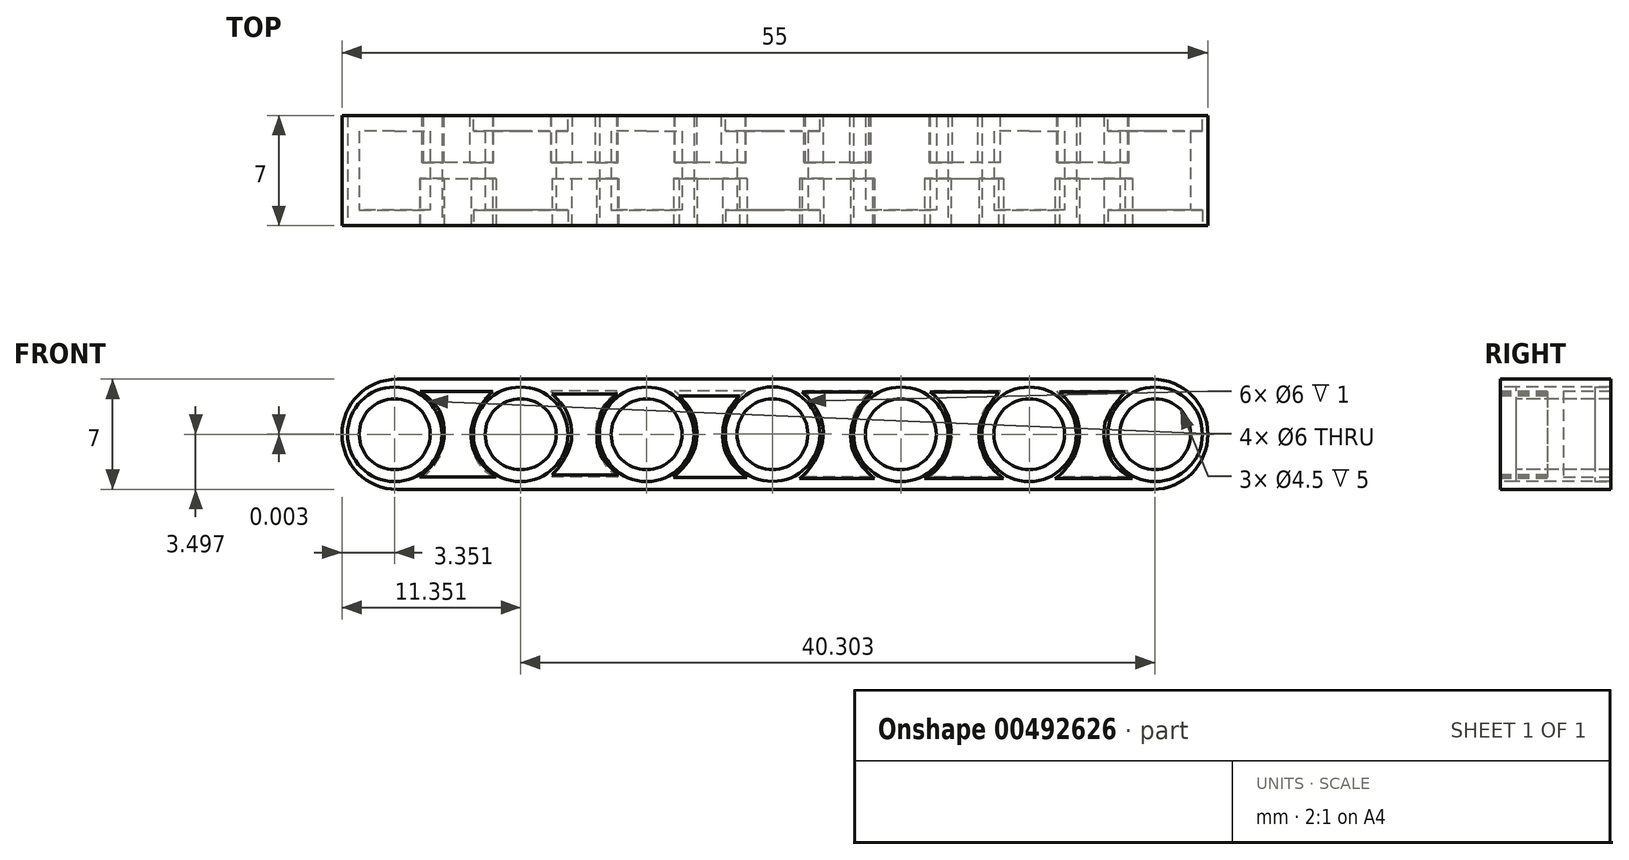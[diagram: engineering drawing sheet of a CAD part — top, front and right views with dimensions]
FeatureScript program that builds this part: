
annotation { "Feature Type Name" : "Feature", "Feature Type Description" : "" }
export const myFeature = defineFeature(function(context is Context, id is Id, definition is map)
    precondition{}
    {
        {
            var Q0;
            Q0=qCreatedBy(makeId("Front.planeOp"),FACE);
            var sketch = newSketch(context, id + "F0", { "sketchPlane" : qUnion([Q0])});
            skLineSegment(sketch, "E0", {"start": v(-51.8, 37) * mm, "end": v(3.2, 37) * mm});
            skLineSegment(sketch, "E1", {"start": v(3.2, 37) * mm, "end": v(3.2, 30) * mm});
            skLineSegment(sketch, "E2", {"start": v(3.2, 30) * mm, "end": v(-51.8, 30) * mm});
            skLineSegment(sketch, "E3", {"start": v(-51.8, 30) * mm, "end": v(-51.8, 37) * mm});
            skSolve(sketch);
        }
        {
            var Q0;
            Q0=makeQuery(id+"F0.imprint","IMPRINT",FACE,{"disambiguationData":[TD([[makeQuery(id+"F0.imprint","IMPRINT",EDGE,{"derivedFrom":sQuery(id+"F0.wireOp",EDGE,"E0")}),-1.0]])]});
            extrude(context, id + "F1", {"entities" : qUnion([Q0]), "depth" : 7 * mm});
        }
        {
            var Q0;
            Q0=makeQuery(id+"F1.opExtrude","CAP_FACE",FACE,{"disambiguationData":[OSD([sQuery(id+"F0.wireOp",EDGE,"E0"),sQuery(id+"F0.wireOp",EDGE,"E1"),sQuery(id+"F0.wireOp",EDGE,"E2"),sQuery(id+"F0.wireOp",EDGE,"E3")])],"isStart":false});
            var sketch = newSketch(context, id + "F2", { "sketchPlane" : qUnion([Q0])});
            skPoint(sketch, "E4.startSnap0", {"position": v(-51.8, 33.5) * mm});
            skCircle(sketch, "E5.MirrorC", {"center": v(-0.16, 33.5) * mm, "radius": 2.25 * mm});
            skCircle(sketch, "E6.MirrorC", {"center": v(-16.3, 33.5) * mm, "radius": 2.25 * mm});
            skCircle(sketch, "E7.MirrorC", {"center": v(-24.46, 33.5) * mm, "radius": 2.25 * mm});
            skCircle(sketch, "E8.MirrorC", {"center": v(-32.46, 33.5) * mm, "radius": 2.25 * mm});
            skCircle(sketch, "E9.MirrorC", {"center": v(-40.46, 33.5) * mm, "radius": 2.25 * mm});
            skCircle(sketch, "E10.MirrorC", {"center": v(-48.46, 33.5) * mm, "radius": 2.25 * mm});
            skCircle(sketch, "E11.MirrorC", {"center": v(-8.16, 33.5) * mm, "radius": 2.25 * mm});
            skCircle(sketch, "E12", {"center": v(-0.16, 33.5) * mm, "radius": 3 * mm});
            skCircle(sketch, "E13", {"center": v(-8.16, 33.5) * mm, "radius": 3 * mm});
            skCircle(sketch, "E14", {"center": v(-16.3, 33.5) * mm, "radius": 3 * mm});
            skCircle(sketch, "E15", {"center": v(-24.46, 33.5) * mm, "radius": 3 * mm});
            skCircle(sketch, "E16", {"center": v(-32.46, 33.5) * mm, "radius": 3 * mm});
            skCircle(sketch, "E17", {"center": v(-40.46, 33.5) * mm, "radius": 3 * mm});
            skCircle(sketch, "E18", {"center": v(-48.46, 33.5) * mm, "radius": 3 * mm});
            skSolve(sketch);
        }
        {
            var Q0;
            Q0=makeQuery(id+"F2.imprint","IMPRINT",FACE,{"disambiguationData":[TD([[makeQuery(id+"F2.imprint","IMPRINT",EDGE,{"derivedFrom":sQuery(id+"F2.wireOp",EDGE,"E10.MirrorC")}),-1.0]])]});
            var Q1;
            Q1=makeQuery(id+"F2.imprint","IMPRINT",FACE,{"disambiguationData":[TD([[makeQuery(id+"F2.imprint","IMPRINT",EDGE,{"derivedFrom":sQuery(id+"F2.wireOp",EDGE,"E9.MirrorC")}),1.0]])]});
            var Q2;
            Q2=makeQuery(id+"F2.imprint","IMPRINT",FACE,{"disambiguationData":[TD([[makeQuery(id+"F2.imprint","IMPRINT",EDGE,{"derivedFrom":sQuery(id+"F2.wireOp",EDGE,"E8.MirrorC")}),-1.0]])]});
            var Q3;
            Q3=makeQuery(id+"F2.imprint","IMPRINT",FACE,{"disambiguationData":[TD([[makeQuery(id+"F2.imprint","IMPRINT",EDGE,{"derivedFrom":sQuery(id+"F2.wireOp",EDGE,"E7.MirrorC")}),1.0]])]});
            var Q4;
            Q4=makeQuery(id+"F2.imprint","IMPRINT",FACE,{"disambiguationData":[TD([[makeQuery(id+"F2.imprint","IMPRINT",EDGE,{"derivedFrom":sQuery(id+"F2.wireOp",EDGE,"E6.MirrorC")}),-1.0]])]});
            var Q5;
            Q5=makeQuery(id+"F2.imprint","IMPRINT",FACE,{"disambiguationData":[TD([[makeQuery(id+"F2.imprint","IMPRINT",EDGE,{"derivedFrom":sQuery(id+"F2.wireOp",EDGE,"E11.MirrorC")}),-1.0]])]});
            var Q6;
            Q6=makeQuery(id+"F2.imprint","IMPRINT",FACE,{"disambiguationData":[TD([[makeQuery(id+"F2.imprint","IMPRINT",EDGE,{"derivedFrom":sQuery(id+"F2.wireOp",EDGE,"E5.MirrorC")}),1.0]])]});
            extrude(context, id + "F3", {"entities" : qUnion([Q0, Q1, Q2, Q3, Q4, Q5, Q6]), "operationType" : NewBodyOperationType.REMOVE, "oppositeDirection" : true, "depth" : 8 * mm});
        }
        {
            var Q0;
            Q0=makeQuery(id+"F1.opExtrude","CAP_FACE",FACE,{"disambiguationData":[OSD([sQuery(id+"F0.wireOp",EDGE,"E0"),sQuery(id+"F0.wireOp",EDGE,"E1"),sQuery(id+"F0.wireOp",EDGE,"E2"),sQuery(id+"F0.wireOp",EDGE,"E3")])],"isStart":false});
            var sketch = newSketch(context, id + "F4", { "sketchPlane" : qUnion([Q0])});
            skSolve(sketch);
        }
        {
            var Q0;
            Q0=makeQuery(id+"F1.opExtrude","SWEPT_EDGE",EDGE,{"disambiguationData":[OSD([sQuery(id+"F0.wireOp",EDGE,"E1"),sQuery(id+"F0.wireOp",EDGE,"E2")])]});
            var Q1;
            Q1=makeQuery(id+"F1.opExtrude","SWEPT_EDGE",EDGE,{"disambiguationData":[OSD([sQuery(id+"F0.wireOp",EDGE,"E0"),sQuery(id+"F0.wireOp",EDGE,"E1")])]});
            var Q2;
            Q2=makeQuery(id+"F1.opExtrude","SWEPT_EDGE",EDGE,{"disambiguationData":[OSD([sQuery(id+"F0.wireOp",EDGE,"E2"),sQuery(id+"F0.wireOp",EDGE,"E3")])]});
            var Q3;
            Q3=makeQuery(id+"F1.opExtrude","SWEPT_EDGE",EDGE,{"disambiguationData":[OSD([sQuery(id+"F0.wireOp",EDGE,"E0"),sQuery(id+"F0.wireOp",EDGE,"E3")])]});
            fillet(context, id + "F5", {"entities" : qUnion([Q0, Q1, Q2, Q3]), "radius" : 3.5 * mm, "tangentPropagation" : true, "allowEdgeOverflow" : false});
        }
        {
            var Q0;
            Q0=makeQuery(id+"F2.imprint","IMPRINT",FACE,{"disambiguationData":[TD([[makeQuery(id+"F2.imprint","IMPRINT",EDGE,{"derivedFrom":sQuery(id+"F2.wireOp",EDGE,"E10.MirrorC")}),1.0]])]});
            var Q1;
            Q1=makeQuery(id+"F2.imprint","IMPRINT",FACE,{"disambiguationData":[TD([[makeQuery(id+"F2.imprint","IMPRINT",EDGE,{"derivedFrom":sQuery(id+"F2.wireOp",EDGE,"E9.MirrorC")}),-1.0]])]});
            var Q2;
            Q2=makeQuery(id+"F2.imprint","IMPRINT",FACE,{"disambiguationData":[TD([[makeQuery(id+"F2.imprint","IMPRINT",EDGE,{"derivedFrom":sQuery(id+"F2.wireOp",EDGE,"E8.MirrorC")}),1.0]])]});
            var Q3;
            Q3=makeQuery(id+"F2.imprint","IMPRINT",FACE,{"disambiguationData":[TD([[makeQuery(id+"F2.imprint","IMPRINT",EDGE,{"derivedFrom":sQuery(id+"F2.wireOp",EDGE,"E7.MirrorC")}),-1.0]])]});
            var Q4;
            Q4=makeQuery(id+"F2.imprint","IMPRINT",FACE,{"disambiguationData":[TD([[makeQuery(id+"F2.imprint","IMPRINT",EDGE,{"derivedFrom":sQuery(id+"F2.wireOp",EDGE,"E6.MirrorC")}),1.0]])]});
            var Q5;
            Q5=makeQuery(id+"F2.imprint","IMPRINT",FACE,{"disambiguationData":[TD([[makeQuery(id+"F2.imprint","IMPRINT",EDGE,{"derivedFrom":sQuery(id+"F2.wireOp",EDGE,"E11.MirrorC")}),1.0]])]});
            var Q6;
            Q6=makeQuery(id+"F2.imprint","IMPRINT",FACE,{"disambiguationData":[TD([[makeQuery(id+"F2.imprint","IMPRINT",EDGE,{"derivedFrom":sQuery(id+"F2.wireOp",EDGE,"E5.MirrorC")}),-1.0]])]});
            extrude(context, id + "F6", {"entities" : qUnion([Q0, Q1, Q2, Q3, Q4, Q5, Q6]), "operationType" : NewBodyOperationType.REMOVE, "oppositeDirection" : true, "depth" : 1 * mm});
        }
        {
            var Q0;
            Q0=makeQuery(id+"F4.imprint","IMPRINT",FACE,{"disambiguationData":[TD([[makeQuery(id+"F4.imprint","IMPRINT",EDGE,{"derivedFrom":makeQuery(id+"F1.opExtrude","CAP_EDGE",EDGE,{"disambiguationData":[OSD([sQuery(id+"F0.wireOp",EDGE,"E0")])],"isStart":false})}),-1.0]])]});
            var sketch = newSketch(context, id + "F7", { "sketchPlane" : qUnion([Q0])});
            skFitSpline(sketch, "E19", {"points": [v(-46.86, 36.21) * mm, v(-45.64, 35.05) * mm, v(-45.45, 32.7) * mm, v(-46.88, 30.8) * mm], "startDerivative": vector(4.15, -3) * mm, "endDerivative": vector(-5.46, -4.25) * mm});
            skLineSegment(sketch, "E20", {"start": v(-46.88, 30.8) * mm, "end": v(-42.03, 30.8) * mm});
            skFitSpline(sketch, "E21", {"points": [v(-42.03, 30.8) * mm, v(-43.47, 32.56) * mm, v(-43.46, 34.37) * mm, v(-42.25, 36.21) * mm], "startDerivative": vector(-7.28, 5.78) * mm, "endDerivative": vector(3.75, 3.53) * mm});
            skLineSegment(sketch, "E22", {"start": v(-46.86, 36.21) * mm, "end": v(-42.25, 36.21) * mm});
            skPoint(sketch, "E23", {"position": v(-44.55, 36.21) * mm});
            skLineSegment(sketch, "E24", {"start": v(-38.45, 36.06) * mm, "end": v(-34.32, 36.06) * mm});
            skFitSpline(sketch, "E25", {"points": [v(-38.45, 36.06) * mm, v(-37.53, 34.94) * mm, v(-37.27, 32.96) * mm, v(-37.97, 31.5) * mm, v(-38.45, 30.93) * mm], "startDerivative": vector(3.64, -3.87) * mm, "endDerivative": vector(-2.13, -2.43) * mm});
            skLineSegment(sketch, "E26", {"start": v(-38.45, 30.93) * mm, "end": v(-34.23, 30.9) * mm});
            skFitSpline(sketch, "E27", {"points": [v(-34.32, 36.06) * mm, v(-35.1, 35.31) * mm, v(-35.55, 34.06) * mm, v(-35.42, 32.3) * mm, v(-34.23, 30.9) * mm], "startDerivative": vector(-3.73, -2.84) * mm, "endDerivative": vector(4.2, -4.01) * mm});
            skFitSpline(sketch, "E28", {"points": [v(-30.38, 35.95) * mm, v(-29.51, 34.78) * mm, v(-29.26, 33.27) * mm, v(-29.7, 31.95) * mm, v(-30.74, 30.75) * mm], "startDerivative": vector(4.04, -4.37) * mm, "endDerivative": vector(-4.5, -4.47) * mm});
            skLineSegment(sketch, "E29", {"start": v(-30.74, 30.75) * mm, "end": v(-26.09, 30.75) * mm});
            skFitSpline(sketch, "E30", {"points": [v(-26.09, 30.75) * mm, v(-27.12, 31.76) * mm, v(-27.61, 33.2) * mm, v(-27.32, 34.88) * mm, v(-26.54, 35.95) * mm], "startDerivative": vector(-4.6, 3.78) * mm, "endDerivative": vector(3.68, 4.1) * mm});
            skLineSegment(sketch, "E31", {"start": v(-30.38, 35.95) * mm, "end": v(-26.54, 35.95) * mm});
            skLineSegment(sketch, "E32", {"start": v(-22.73, 30.7) * mm, "end": v(-17.97, 30.7) * mm});
            skLineSegment(sketch, "E33", {"start": v(-22.58, 36.2) * mm, "end": v(-18.1, 36.2) * mm});
            skFitSpline(sketch, "E34", {"points": [v(-22.58, 36.2) * mm, v(-21.75, 35.23) * mm, v(-21.22, 33.54) * mm, v(-21.97, 31.52) * mm, v(-22.73, 30.7) * mm], "startDerivative": vector(3.8, -3.85) * mm, "endDerivative": vector(-3.57, -3.2) * mm});
            skFitSpline(sketch, "E35", {"points": [v(-17.97, 30.7) * mm, v(-19.14, 32) * mm, v(-19.48, 33.76) * mm, v(-18.8, 35.42) * mm, v(-18.1, 36.2) * mm], "startDerivative": vector(-5.01, 4.55) * mm, "endDerivative": vector(3.45, 3.3) * mm});
            skLineSegment(sketch, "E36", {"start": v(-14.45, 36.2) * mm, "end": v(-10.1, 36.2) * mm});
            skLineSegment(sketch, "E37", {"start": v(-14.82, 30.7) * mm, "end": v(-9.8, 30.7) * mm});
            skFitSpline(sketch, "E38", {"points": [v(-14.45, 36.2) * mm, v(-13.73, 35.48) * mm, v(-13.14, 33.82) * mm, v(-13.7, 31.67) * mm, v(-14.82, 30.7) * mm], "startDerivative": vector(3.72, -3.06) * mm, "endDerivative": vector(-5, -3.27) * mm});
            skFitSpline(sketch, "E39", {"points": [v(-9.8, 30.7) * mm, v(-10.8, 31.73) * mm, v(-11.34, 33.74) * mm, v(-10.66, 35.43) * mm, v(-10.1, 36.2) * mm], "startDerivative": vector(-4.4, 3.63) * mm, "endDerivative": vector(2.68, 3.5) * mm});
            skLineSegment(sketch, "E40", {"start": v(-6.24, 36.2) * mm, "end": v(-2.06, 36.2) * mm});
            skLineSegment(sketch, "E41", {"start": v(-6.5, 30.7) * mm, "end": v(-1.6, 30.7) * mm});
            skFitSpline(sketch, "E42", {"points": [v(-6.24, 36.2) * mm, v(-5.25, 34.9) * mm, v(-5.01, 32.99) * mm, v(-5.74, 31.43) * mm, v(-6.5, 30.7) * mm], "startDerivative": vector(4.42, -4.6) * mm, "endDerivative": vector(-3.8, -3.09) * mm});
            skFitSpline(sketch, "E43", {"points": [v(-1.6, 30.7) * mm, v(-2.57, 31.38) * mm, v(-3.25, 32.6) * mm, v(-3.32, 34.3) * mm, v(-2.06, 36.2) * mm], "startDerivative": vector(-4.81, 2.8) * mm, "endDerivative": vector(5.34, 6.23) * mm});
            skSolve(sketch);
        }
        {
            var Q0;
            Q0=makeQuery(id+"F7.imprint","IMPRINT",FACE,{"disambiguationData":[TD([[makeQuery(id+"F7.imprint","IMPRINT",EDGE,{"derivedFrom":sQuery(id+"F7.wireOp",EDGE,"E19")}),1.0]])]});
            var Q1;
            Q1=makeQuery(id+"F7.imprint","IMPRINT",FACE,{"disambiguationData":[TD([[makeQuery(id+"F7.imprint","IMPRINT",EDGE,{"derivedFrom":sQuery(id+"F7.wireOp",EDGE,"E24")}),-1.0]])]});
            var Q2;
            Q2=makeQuery(id+"F7.imprint","IMPRINT",FACE,{"disambiguationData":[TD([[makeQuery(id+"F7.imprint","IMPRINT",EDGE,{"derivedFrom":sQuery(id+"F7.wireOp",EDGE,"E28")}),1.0]])]});
            var Q3;
            Q3=makeQuery(id+"F7.imprint","IMPRINT",FACE,{"disambiguationData":[TD([[makeQuery(id+"F7.imprint","IMPRINT",EDGE,{"derivedFrom":sQuery(id+"F7.wireOp",EDGE,"E32")}),1.0]])]});
            var Q4;
            Q4=makeQuery(id+"F7.imprint","IMPRINT",FACE,{"disambiguationData":[TD([[makeQuery(id+"F7.imprint","IMPRINT",EDGE,{"derivedFrom":sQuery(id+"F7.wireOp",EDGE,"E40")}),-1.0]])]});
            var Q5;
            Q5=makeQuery(id+"F7.imprint","IMPRINT",FACE,{"disambiguationData":[TD([[makeQuery(id+"F7.imprint","IMPRINT",EDGE,{"derivedFrom":sQuery(id+"F7.wireOp",EDGE,"E36")}),-1.0]])]});
            extrude(context, id + "F8", {"entities" : qUnion([Q0, Q1, Q2, Q3, Q4, Q5]), "operationType" : NewBodyOperationType.REMOVE, "oppositeDirection" : true, "depth" : 3 * mm, "offsetDistance" : 25 * mm});
        }
        {
            var Q0;
            Q0=makeQuery(id+"F1.opExtrude","CAP_FACE",FACE,{"disambiguationData":[OSD([sQuery(id+"F0.wireOp",EDGE,"E0"),sQuery(id+"F0.wireOp",EDGE,"E1"),sQuery(id+"F0.wireOp",EDGE,"E2"),sQuery(id+"F0.wireOp",EDGE,"E3")])],"isStart":true});
            var sketch = newSketch(context, id + "F9", { "sketchPlane" : qUnion([Q0])});
            skPoint(sketch, "E44", {"position": v(0.16, 33.5) * mm});
            skPoint(sketch, "E45", {"position": v(8.16, 33.5) * mm});
            skPoint(sketch, "E46", {"position": v(16.3, 33.5) * mm});
            skPoint(sketch, "E47", {"position": v(24.46, 33.5) * mm});
            skPoint(sketch, "E48", {"position": v(32.46, 33.5) * mm});
            skPoint(sketch, "E49", {"position": v(40.46, 33.5) * mm});
            skPoint(sketch, "E50", {"position": v(48.46, 33.5) * mm});
            skCircle(sketch, "E51", {"center": v(0.16, 33.5) * mm, "radius": 3 * mm});
            skCircle(sketch, "E52", {"center": v(8.16, 33.5) * mm, "radius": 3 * mm});
            skCircle(sketch, "E53", {"center": v(16.3, 33.5) * mm, "radius": 3 * mm});
            skCircle(sketch, "E54", {"center": v(24.46, 33.5) * mm, "radius": 3 * mm});
            skCircle(sketch, "E55", {"center": v(32.46, 33.5) * mm, "radius": 3 * mm});
            skCircle(sketch, "E56", {"center": v(40.46, 33.5) * mm, "radius": 3 * mm});
            skCircle(sketch, "E57", {"center": v(48.46, 33.5) * mm, "radius": 3 * mm});
            skSolve(sketch);
        }
        {
            var Q0;
            Q0=makeQuery(id+"F9.imprint","IMPRINT",FACE,{"disambiguationData":[TD([[makeQuery(id+"F9.imprint","IMPRINT",EDGE,{"derivedFrom":sQuery(id+"F9.wireOp",EDGE,"E51")}),1.0]])]});
            var Q1;
            Q1=makeQuery(id+"F9.imprint","IMPRINT",FACE,{"disambiguationData":[TD([[makeQuery(id+"F9.imprint","IMPRINT",EDGE,{"derivedFrom":sQuery(id+"F9.wireOp",EDGE,"E52")}),1.0]])]});
            var Q2;
            Q2=makeQuery(id+"F9.imprint","IMPRINT",FACE,{"disambiguationData":[TD([[makeQuery(id+"F9.imprint","IMPRINT",EDGE,{"derivedFrom":sQuery(id+"F9.wireOp",EDGE,"E53")}),1.0]])]});
            var Q3;
            Q3=makeQuery(id+"F9.imprint","IMPRINT",FACE,{"disambiguationData":[TD([[makeQuery(id+"F9.imprint","IMPRINT",EDGE,{"derivedFrom":sQuery(id+"F9.wireOp",EDGE,"E54")}),1.0]])]});
            var Q4;
            Q4=makeQuery(id+"F9.imprint","IMPRINT",FACE,{"disambiguationData":[TD([[makeQuery(id+"F9.imprint","IMPRINT",EDGE,{"derivedFrom":sQuery(id+"F9.wireOp",EDGE,"E55")}),1.0]])]});
            var Q5;
            Q5=makeQuery(id+"F9.imprint","IMPRINT",FACE,{"disambiguationData":[TD([[makeQuery(id+"F9.imprint","IMPRINT",EDGE,{"derivedFrom":sQuery(id+"F9.wireOp",EDGE,"E56")}),1.0]])]});
            var Q6;
            Q6=makeQuery(id+"F9.imprint","IMPRINT",FACE,{"disambiguationData":[TD([[makeQuery(id+"F9.imprint","IMPRINT",EDGE,{"derivedFrom":sQuery(id+"F9.wireOp",EDGE,"E57")}),1.0]])]});
            extrude(context, id + "F10", {"entities" : qUnion([Q0, Q1, Q2, Q3, Q4, Q5, Q6]), "operationType" : NewBodyOperationType.REMOVE, "oppositeDirection" : true, "depth" : 1 * mm});
        }
        {
            var Q0;
            Q0=makeQuery(id+"F1.opExtrude","CAP_FACE",FACE,{"disambiguationData":[OSD([sQuery(id+"F0.wireOp",EDGE,"E0"),sQuery(id+"F0.wireOp",EDGE,"E1"),sQuery(id+"F0.wireOp",EDGE,"E2"),sQuery(id+"F0.wireOp",EDGE,"E3")])],"isStart":true});
            var sketch = newSketch(context, id + "F11", { "sketchPlane" : qUnion([Q0])});
            skLineSegment(sketch, "E58", {"start": v(1.9, 36.24) * mm, "end": v(6.4, 36.24) * mm});
            skLineSegment(sketch, "E59", {"start": v(1.81, 30.78) * mm, "end": v(6.34, 30.78) * mm});
            skFitSpline(sketch, "E60", {"points": [v(1.9, 36.24) * mm, v(2.8, 35.34) * mm, v(3.37, 33.62) * mm, v(2.73, 31.58) * mm, v(1.81, 30.78) * mm], "startDerivative": vector(4.25, -3.54) * mm, "endDerivative": vector(-4.45, -2.82) * mm});
            skFitSpline(sketch, "E61", {"points": [v(6.34, 30.78) * mm, v(5.62, 31.51) * mm, v(4.96, 33.23) * mm, v(5.07, 34.48) * mm, v(6.4, 36.24) * mm], "startDerivative": vector(-3.7, 2.88) * mm, "endDerivative": vector(5.5, 6.1) * mm});
            skLineSegment(sketch, "E62", {"start": v(10, 36.24) * mm, "end": v(14.44, 36.24) * mm});
            skLineSegment(sketch, "E63", {"start": v(10, 30.78) * mm, "end": v(14.49, 30.78) * mm});
            skFitSpline(sketch, "E64", {"points": [v(10, 36.24) * mm, v(10.9, 35.23) * mm, v(11.4, 33.3) * mm, v(10, 30.78) * mm], "startDerivative": vector(3.46, -3.23) * mm, "endDerivative": vector(-4.88, -6.29) * mm});
            skFitSpline(sketch, "E65", {"points": [v(14.49, 30.78) * mm, v(13.65, 31.64) * mm, v(13.03, 33.5) * mm, v(13.58, 35.34) * mm, v(14.44, 36.24) * mm], "startDerivative": vector(-3.96, 3.32) * mm, "endDerivative": vector(4.05, 3.46) * mm});
            skLineSegment(sketch, "E66", {"start": v(18.34, 36.24) * mm, "end": v(22.37, 36.24) * mm});
            skLineSegment(sketch, "E67", {"start": v(18.2, 30.78) * mm, "end": v(22.45, 30.78) * mm});
            skFitSpline(sketch, "E68", {"points": [v(18.34, 36.24) * mm, v(19.22, 34.95) * mm, v(19.5, 33.25) * mm, v(18.91, 31.58) * mm, v(18.2, 30.78) * mm], "startDerivative": vector(3.9, -4.8) * mm, "endDerivative": vector(-3.56, -3.24) * mm});
            skFitSpline(sketch, "E69", {"points": [v(22.45, 30.78) * mm, v(21.7, 31.89) * mm, v(21.22, 33.3) * mm, v(21.51, 34.88) * mm, v(22.37, 36.24) * mm], "startDerivative": vector(-3.29, 4.5) * mm, "endDerivative": vector(3.73, 5.02) * mm});
            skLineSegment(sketch, "E70", {"start": v(26.18, 36.24) * mm, "end": v(30.69, 36.24) * mm});
            skLineSegment(sketch, "E71", {"start": v(26.13, 30.78) * mm, "end": v(30.66, 30.78) * mm});
            skFitSpline(sketch, "E72", {"points": [v(26.18, 36.24) * mm, v(27.39, 34.9) * mm, v(27.63, 32.99) * mm, v(26.88, 31.45) * mm, v(26.13, 30.78) * mm], "startDerivative": vector(5.25, -4.5) * mm, "endDerivative": vector(-3.8, -2.83) * mm});
            skFitSpline(sketch, "E73", {"points": [v(30.66, 30.78) * mm, v(29.87, 31.62) * mm, v(29.3, 33) * mm, v(29.54, 34.95) * mm, v(30.69, 36.24) * mm], "startDerivative": vector(-3.89, 3.58) * mm, "endDerivative": vector(5.06, 4.35) * mm});
            skLineSegment(sketch, "E74", {"start": v(34.35, 36.24) * mm, "end": v(38.53, 36.24) * mm});
            skLineSegment(sketch, "E75", {"start": v(34.27, 30.78) * mm, "end": v(38.5, 30.78) * mm});
            skFitSpline(sketch, "E76", {"points": [v(34.35, 36.24) * mm, v(35.47, 34.87) * mm, v(35.65, 33.12) * mm, v(35.08, 31.55) * mm, v(34.27, 30.78) * mm], "startDerivative": vector(5, -4.77) * mm, "endDerivative": vector(-4.11, -3.09) * mm});
            skFitSpline(sketch, "E77", {"points": [v(38.5, 30.78) * mm, v(37.85, 31.57) * mm, v(37.2, 33.14) * mm, v(37.49, 34.98) * mm, v(38.53, 36.24) * mm], "startDerivative": vector(-3.2, 3.45) * mm, "endDerivative": vector(4.6, 4.43) * mm});
            skLineSegment(sketch, "E78", {"start": v(42.21, 36.24) * mm, "end": v(46.72, 36.24) * mm});
            skLineSegment(sketch, "E79", {"start": v(42.18, 30.78) * mm, "end": v(46.62, 30.78) * mm});
            skFitSpline(sketch, "E80", {"points": [v(42.21, 36.24) * mm, v(43.2, 35.14) * mm, v(43.64, 33.08) * mm, v(43.01, 31.5) * mm, v(42.18, 30.78) * mm], "startDerivative": vector(4.5, -3.89) * mm, "endDerivative": vector(-4.2, -2.9) * mm});
            skFitSpline(sketch, "E81", {"points": [v(46.72, 36.24) * mm, v(45.77, 35.24) * mm, v(45.34, 33.67) * mm, v(45.64, 32.04) * mm, v(46.62, 30.78) * mm], "startDerivative": vector(-4.47, -3.8) * mm, "endDerivative": vector(4.45, -4.62) * mm});
            skSolve(sketch);
        }
        {
            var Q0;
            Q0=makeQuery(id+"F11.imprint","IMPRINT",FACE,{"disambiguationData":[TD([[makeQuery(id+"F11.imprint","IMPRINT",EDGE,{"derivedFrom":sQuery(id+"F11.wireOp",EDGE,"E58")}),-1.0]])]});
            var Q1;
            Q1=makeQuery(id+"F11.imprint","IMPRINT",FACE,{"disambiguationData":[TD([[makeQuery(id+"F11.imprint","IMPRINT",EDGE,{"derivedFrom":sQuery(id+"F11.wireOp",EDGE,"E62")}),-1.0]])]});
            var Q2;
            Q2=makeQuery(id+"F11.imprint","IMPRINT",FACE,{"disambiguationData":[TD([[makeQuery(id+"F11.imprint","IMPRINT",EDGE,{"derivedFrom":sQuery(id+"F11.wireOp",EDGE,"E66")}),-1.0]])]});
            var Q3;
            Q3=makeQuery(id+"F11.imprint","IMPRINT",FACE,{"disambiguationData":[TD([[makeQuery(id+"F11.imprint","IMPRINT",EDGE,{"derivedFrom":sQuery(id+"F11.wireOp",EDGE,"E70")}),-1.0]])]});
            var Q4;
            Q4=makeQuery(id+"F11.imprint","IMPRINT",FACE,{"disambiguationData":[TD([[makeQuery(id+"F11.imprint","IMPRINT",EDGE,{"derivedFrom":sQuery(id+"F11.wireOp",EDGE,"E74")}),-1.0]])]});
            var Q5;
            Q5=makeQuery(id+"F11.imprint","IMPRINT",FACE,{"disambiguationData":[TD([[makeQuery(id+"F11.imprint","IMPRINT",EDGE,{"derivedFrom":sQuery(id+"F11.wireOp",EDGE,"E78")}),-1.0]])]});
            extrude(context, id + "F12", {"entities" : qUnion([Q0, Q1, Q2, Q3, Q4, Q5]), "operationType" : NewBodyOperationType.REMOVE, "oppositeDirection" : true, "depth" : 3 * mm});
        }
    });
